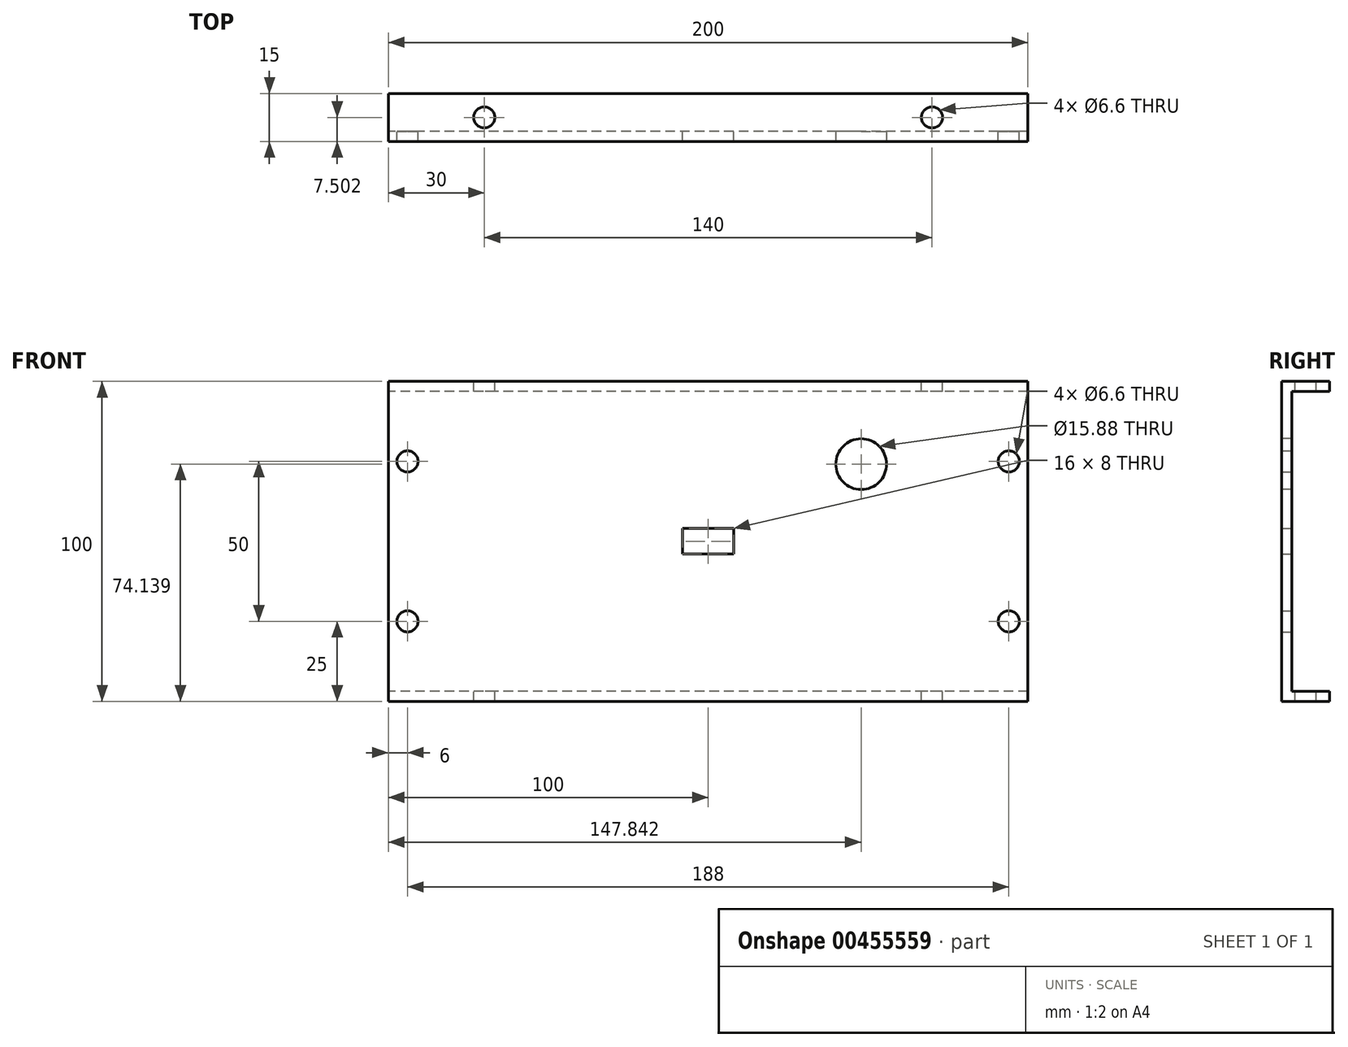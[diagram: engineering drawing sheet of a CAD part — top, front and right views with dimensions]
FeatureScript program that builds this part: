
annotation { "Feature Type Name" : "Feature", "Feature Type Description" : "" }
export const myFeature = defineFeature(function(context is Context, id is Id, definition is map)
    precondition{}
    {
        {
            var Q0;
            Q0=qCreatedBy(makeId("Right.planeOp"),FACE);
            var sketch = newSketch(context, id + "F0", { "sketchPlane" : qUnion([Q0])});
            skLineSegment(sketch, "E0.bottom", {"start": v(1.59, 50) * mm, "end": v(-1.59, 50) * mm});
            skLineSegment(sketch, "E0.top", {"start": v(1.59, -50) * mm, "end": v(-1.59, -50) * mm});
            skLineSegment(sketch, "E0.left", {"start": v(1.59, 46.83) * mm, "end": v(1.59, -46.83) * mm});
            skLineSegment(sketch, "E0.right", {"start": v(-1.59, 50) * mm, "end": v(-1.59, -50) * mm});
            skPoint(sketch, "E0.middle", {"position": v(0, 0) * mm});
            skLineSegment(sketch, "E1.bottom", {"start": v(-1.59, -50) * mm, "end": v(13.41, -50) * mm});
            skLineSegment(sketch, "E1.top", {"start": v(1.59, -46.83) * mm, "end": v(13.41, -46.83) * mm});
            skLineSegment(sketch, "E1.left", {"start": v(-1.59, -50) * mm, "end": v(-1.59, -46.83) * mm});
            skLineSegment(sketch, "E1.right", {"start": v(13.41, -50) * mm, "end": v(13.41, -46.83) * mm});
            skLineSegment(sketch, "E2.bottom", {"start": v(-1.59, 50) * mm, "end": v(13.41, 50) * mm});
            skLineSegment(sketch, "E2.top", {"start": v(1.59, 46.83) * mm, "end": v(13.41, 46.83) * mm});
            skLineSegment(sketch, "E2.left", {"start": v(-1.59, 50) * mm, "end": v(-1.59, 46.83) * mm});
            skLineSegment(sketch, "E2.right", {"start": v(13.41, 50) * mm, "end": v(13.41, 46.83) * mm});
            skSolve(sketch);
        }
        {
            var Q0;
            Q0=makeQuery(id+"F0.imprint","IMPRINT",FACE,{"disambiguationData":[TD([[makeQuery(id+"F0.imprint","IMPRINT",EDGE,{"derivedFrom":sQuery(id+"F0.wireOp",EDGE,"E0.left")}),-1.0]])]});
            extrude(context, id + "F1", {"entities" : qUnion([Q0]), "endBound" : BoundingType.SYMMETRIC, "depth" : 200 * mm});
        }
        {
            var Q0;
            Q0=makeQuery(id+"F1.opExtrude","SWEPT_FACE",FACE,{"disambiguationData":[OSD([sQuery(id+"F0.wireOp",EDGE,"E0.right"),sQuery(id+"F0.wireOp",EDGE,"E1.left"),sQuery(id+"F0.wireOp",EDGE,"E2.left")])]});
            var sketch = newSketch(context, id + "F2", { "sketchPlane" : qUnion([Q0])});
            skLineSegment(sketch, "E3.bottom", {"start": v(8, 4) * mm, "end": v(-8, 4) * mm});
            skLineSegment(sketch, "E3.top", {"start": v(8, -4) * mm, "end": v(-8, -4) * mm});
            skLineSegment(sketch, "E3.left", {"start": v(8, 4) * mm, "end": v(8, -4) * mm});
            skLineSegment(sketch, "E3.right", {"start": v(-8, 4) * mm, "end": v(-8, -4) * mm});
            skPoint(sketch, "E3.middle", {"position": v(0, 0) * mm});
            skCircle(sketch, "E4", {"center": v(94, -25) * mm, "radius": 3.3 * mm});
            skCircle(sketch, "E5.MirrorC", {"center": v(94, 25) * mm, "radius": 3.3 * mm});
            skCircle(sketch, "E6.MirrorC", {"center": v(-94, -25) * mm, "radius": 3.3 * mm});
            skCircle(sketch, "E7.MirrorC", {"center": v(-94, 25) * mm, "radius": 3.3 * mm});
            skSolve(sketch);
        }
        {
            var Q0;
            Q0 = qSketchRegion(id + "F2", true);
            extrude(context, id + "F3", {"entities" : qUnion([Q0]), "operationType" : NewBodyOperationType.REMOVE, "endBound" : BoundingType.THROUGH_ALL, "depth" : 25 * mm, "hasSecondDirection" : true, "secondDirectionBound" : SecondDirectionBoundingType.THROUGH_ALL, "secondDirectionOppositeDirection" : true, "secondDirectionDepth" : 25 * mm});
        }
        {
            var Q0;
            Q0=makeQuery(id+"F1.opExtrude","SWEPT_FACE",FACE,{"disambiguationData":[OSD([sQuery(id+"F0.wireOp",EDGE,"E2.bottom")])]});
            var sketch = newSketch(context, id + "F4", { "sketchPlane" : qUnion([Q0])});
            skCircle(sketch, "E8", {"center": v(-70, 5.91) * mm, "radius": 3.3 * mm});
            skCircle(sketch, "E9.MirrorC", {"center": v(70, 5.91) * mm, "radius": 3.3 * mm});
            skSolve(sketch);
        }
        {
            var Q0;
            Q0 = qSketchRegion(id + "F4", true);
            extrude(context, id + "F5", {"entities" : qUnion([Q0]), "operationType" : NewBodyOperationType.REMOVE, "endBound" : BoundingType.THROUGH_ALL, "oppositeDirection" : true, "depth" : 25 * mm});
        }
        {
            var Q0;
            Q0=makeQuery(id+"F1.opExtrude","SWEPT_FACE",FACE,{"disambiguationData":[OSD([sQuery(id+"F0.wireOp",EDGE,"E0.right"),sQuery(id+"F0.wireOp",EDGE,"E1.left"),sQuery(id+"F0.wireOp",EDGE,"E2.left")])]});
            var sketch = newSketch(context, id + "F6", { "sketchPlane" : qUnion([Q0])});
            skCircle(sketch, "E10", {"center": v(47.84, 24.14) * mm, "radius": 7.94 * mm});
            skSolve(sketch);
        }
        {
            var Q0;
            Q0=makeQuery(id+"F6.imprint","IMPRINT",FACE,{"disambiguationData":[TD([[makeQuery(id+"F6.imprint","IMPRINT",EDGE,{"derivedFrom":sQuery(id+"F6.wireOp",EDGE,"E10")}),1.0]])]});
            extrude(context, id + "F7", {"entities" : qUnion([Q0]), "operationType" : NewBodyOperationType.REMOVE, "endBound" : BoundingType.THROUGH_ALL, "oppositeDirection" : true, "depth" : 25 * mm, "offsetDistance" : 25 * mm});
        }
    });
